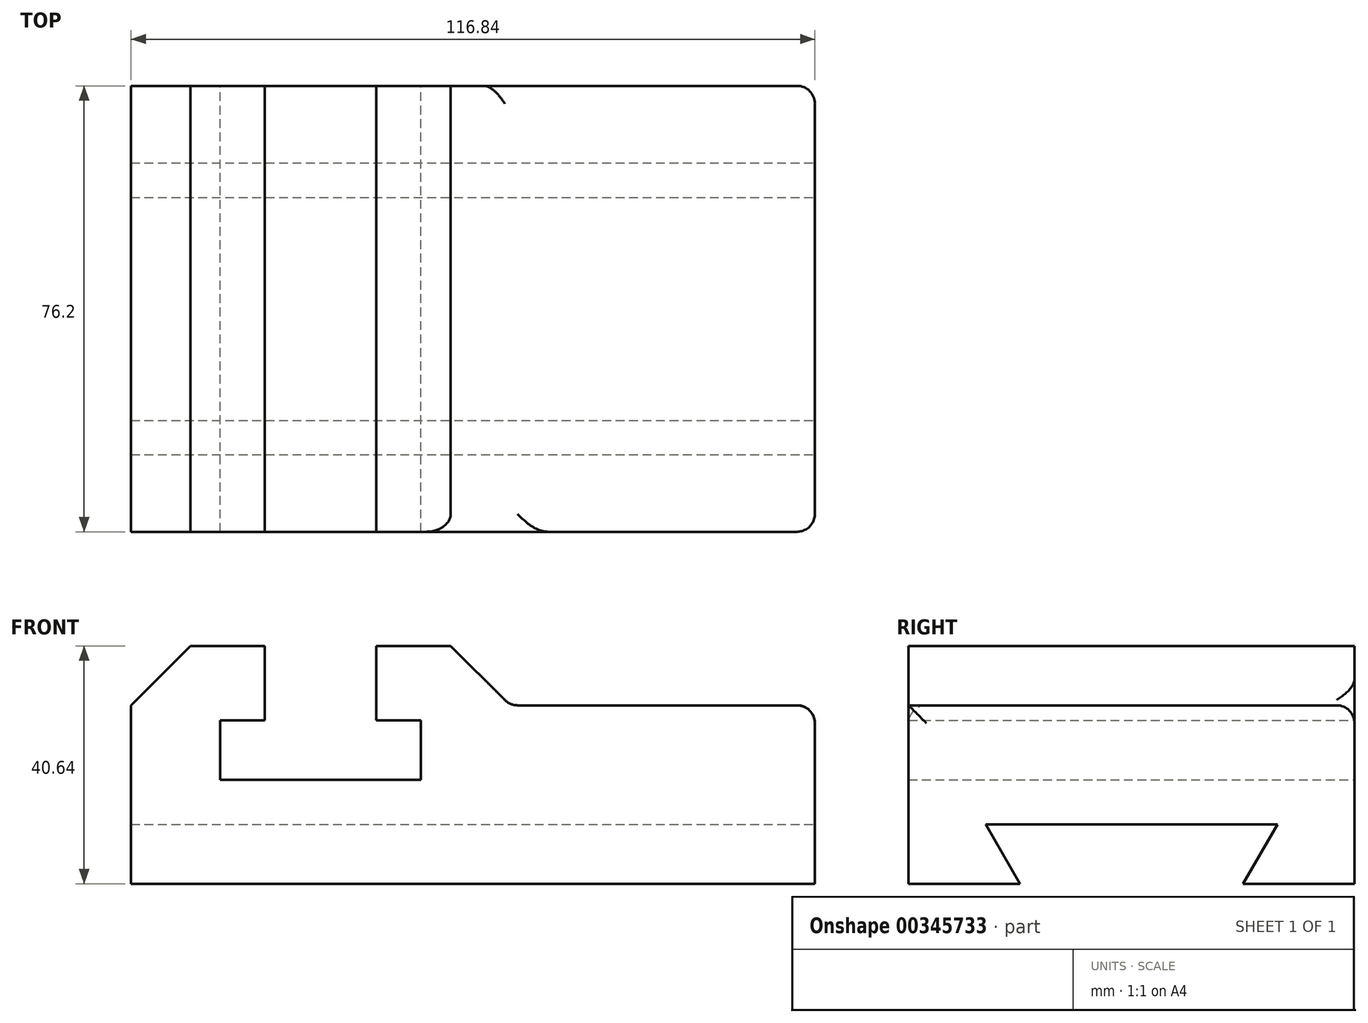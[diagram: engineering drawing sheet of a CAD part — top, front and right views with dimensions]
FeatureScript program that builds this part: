
annotation { "Feature Type Name" : "Feature", "Feature Type Description" : "" }
export const myFeature = defineFeature(function(context is Context, id is Id, definition is map)
    precondition{}
    {
        {
            var Q0;
            Q0=qCreatedBy(makeId("Front.planeOp"),FACE);
            var sketch = newSketch(context, id + "F0", { "sketchPlane" : qUnion([Q0])});
            skLineSegment(sketch, "E0", {"start": v(67.3, -20.28) * mm, "end": v(-49.53, -20.28) * mm});
            skLineSegment(sketch, "E1", {"start": v(-49.53, -20.28) * mm, "end": v(-49.53, 20.36) * mm});
            skLineSegment(sketch, "E2", {"start": v(-49.53, 20.36) * mm, "end": v(-26.67, 20.36) * mm});
            skLineSegment(sketch, "E3", {"start": v(-26.67, 20.36) * mm, "end": v(-26.67, 7.66) * mm});
            skLineSegment(sketch, "E4", {"start": v(-26.67, 7.66) * mm, "end": v(-34.3, 7.66) * mm});
            skLineSegment(sketch, "E5", {"start": v(-34.3, 7.66) * mm, "end": v(-34.3, -2.5) * mm});
            skLineSegment(sketch, "E6", {"start": v(-34.3, -2.5) * mm, "end": v(0, -2.5) * mm});
            skLineSegment(sketch, "E7", {"start": v(0, -2.5) * mm, "end": v(0, 7.66) * mm});
            skLineSegment(sketch, "E8", {"start": v(0, 7.66) * mm, "end": v(-7.62, 7.66) * mm});
            skLineSegment(sketch, "E9", {"start": v(-7.62, 7.66) * mm, "end": v(-7.62, 20.36) * mm});
            skLineSegment(sketch, "E10", {"start": v(-7.62, 20.36) * mm, "end": v(5.08, 20.36) * mm});
            skLineSegment(sketch, "E11", {"start": v(67.3, -20.28) * mm, "end": v(67.3, 10.2) * mm});
            skLineSegment(sketch, "E12", {"start": v(-49.53, 20.36) * mm, "end": v(-49.53, 10.2) * mm});
            skLineSegment(sketch, "E13", {"start": v(-49.53, 20.36) * mm, "end": v(-39.37, 20.36) * mm});
            skLineSegment(sketch, "E14", {"start": v(-39.37, 20.36) * mm, "end": v(-49.53, 10.2) * mm});
            skLineSegment(sketch, "E15", {"start": v(5.08, 20.36) * mm, "end": v(5.08, 10.2) * mm});
            skLineSegment(sketch, "E16", {"start": v(5.08, 10.2) * mm, "end": v(15.24, 10.2) * mm});
            skLineSegment(sketch, "E17", {"start": v(5.08, 20.36) * mm, "end": v(15.24, 10.2) * mm});
            skLineSegment(sketch, "E18", {"start": v(15.24, 10.2) * mm, "end": v(67.3, 10.2) * mm});
            skSolve(sketch);
        }
        {
            var Q0;
            Q0=makeQuery(id+"F0.imprint","IMPRINT",FACE,{"disambiguationData":[TD([[makeQuery(id+"F0.imprint","IMPRINT",EDGE,{"derivedFrom":sQuery(id+"F0.wireOp",EDGE,"E15")}),1.0]])]});
            var Q1;
            Q1=makeQuery(id+"F0.imprint","IMPRINT",FACE,{"disambiguationData":[TD([[makeQuery(id+"F0.imprint","IMPRINT",EDGE,{"derivedFrom":sQuery(id+"F0.wireOp",EDGE,"E0")}),-1.0]])]});
            extrude(context, id + "F1", {"entities" : qUnion([Q0, Q1]), "endBound" : BoundingType.SYMMETRIC, "depth" : 76.2 * mm});
        }
        {
            var Q0;
            Q0=makeQuery(id+"F1.opExtrude","CAP_EDGE",EDGE,{"disambiguationData":[OSD([sQuery(id+"F0.wireOp",EDGE,"E17")])],"isStart":false});
            var Q1;
            Q1=makeQuery(id+"F1.opExtrude","SWEPT_EDGE",EDGE,{"disambiguationData":[OSD([sQuery(id+"F0.wireOp",EDGE,"E16"),sQuery(id+"F0.wireOp",EDGE,"E17"),sQuery(id+"F0.wireOp",EDGE,"E18")])]});
            var Q2;
            Q2=makeQuery(id+"F1.opExtrude","CAP_EDGE",EDGE,{"disambiguationData":[OSD([sQuery(id+"F0.wireOp",EDGE,"E11")])],"isStart":false});
            var Q3;
            Q3=makeQuery(id+"F1.opExtrude","SWEPT_EDGE",EDGE,{"disambiguationData":[OSD([sQuery(id+"F0.wireOp",EDGE,"E11"),sQuery(id+"F0.wireOp",EDGE,"E18")])]});
            var Q4;
            Q4=makeQuery(id+"F1.opExtrude","CAP_EDGE",EDGE,{"disambiguationData":[OSD([sQuery(id+"F0.wireOp",EDGE,"E18")])],"isStart":true});
            var Q5;
            Q5=makeQuery(id+"F1.opExtrude","CAP_EDGE",EDGE,{"disambiguationData":[OSD([sQuery(id+"F0.wireOp",EDGE,"E11")])],"isStart":true});
            fillet(context, id + "F2", {"entities" : qUnion([Q0, Q1, Q2, Q3, Q4, Q5]), "radius" : 3.05 * mm, "tangentPropagation" : true, "allowEdgeOverflow" : false});
        }
        {
            var Q0;
            Q0=makeQuery(id+"F1.opExtrude","SWEPT_FACE",FACE,{"disambiguationData":[OSD([sQuery(id+"F0.wireOp",EDGE,"E11")])]});
            var sketch = newSketch(context, id + "F3", { "sketchPlane" : qUnion([Q0])});
            skLineSegment(sketch, "E19", {"start": v(0, -20.28) * mm, "end": v(-19.05, -20.28) * mm});
            skLineSegment(sketch, "E20", {"start": v(0, -10.12) * mm, "end": v(-24.92, -10.12) * mm});
            skLineSegment(sketch, "E21", {"start": v(-24.92, -10.12) * mm, "end": v(-19.05, -20.28) * mm});
            skLineSegment(sketch, "E22", {"start": v(0, -20.28) * mm, "end": v(19.05, -20.28) * mm});
            skLineSegment(sketch, "E23", {"start": v(19.05, -20.28) * mm, "end": v(24.92, -10.12) * mm});
            skLineSegment(sketch, "E24", {"start": v(24.92, -10.12) * mm, "end": v(0, -10.12) * mm});
            skSolve(sketch);
        }
        {
            var Q0;
            Q0=makeQuery(id+"F3.imprint","IMPRINT",FACE,{"disambiguationData":[TD([[makeQuery(id+"F3.imprint","IMPRINT",EDGE,{"derivedFrom":sQuery(id+"F3.wireOp",EDGE,"E19")}),1.0]])]});
            extrude(context, id + "F4", {"entities" : qUnion([Q0]), "operationType" : NewBodyOperationType.REMOVE, "oppositeDirection" : true, "depth" : 116.84 * mm});
        }
    });
